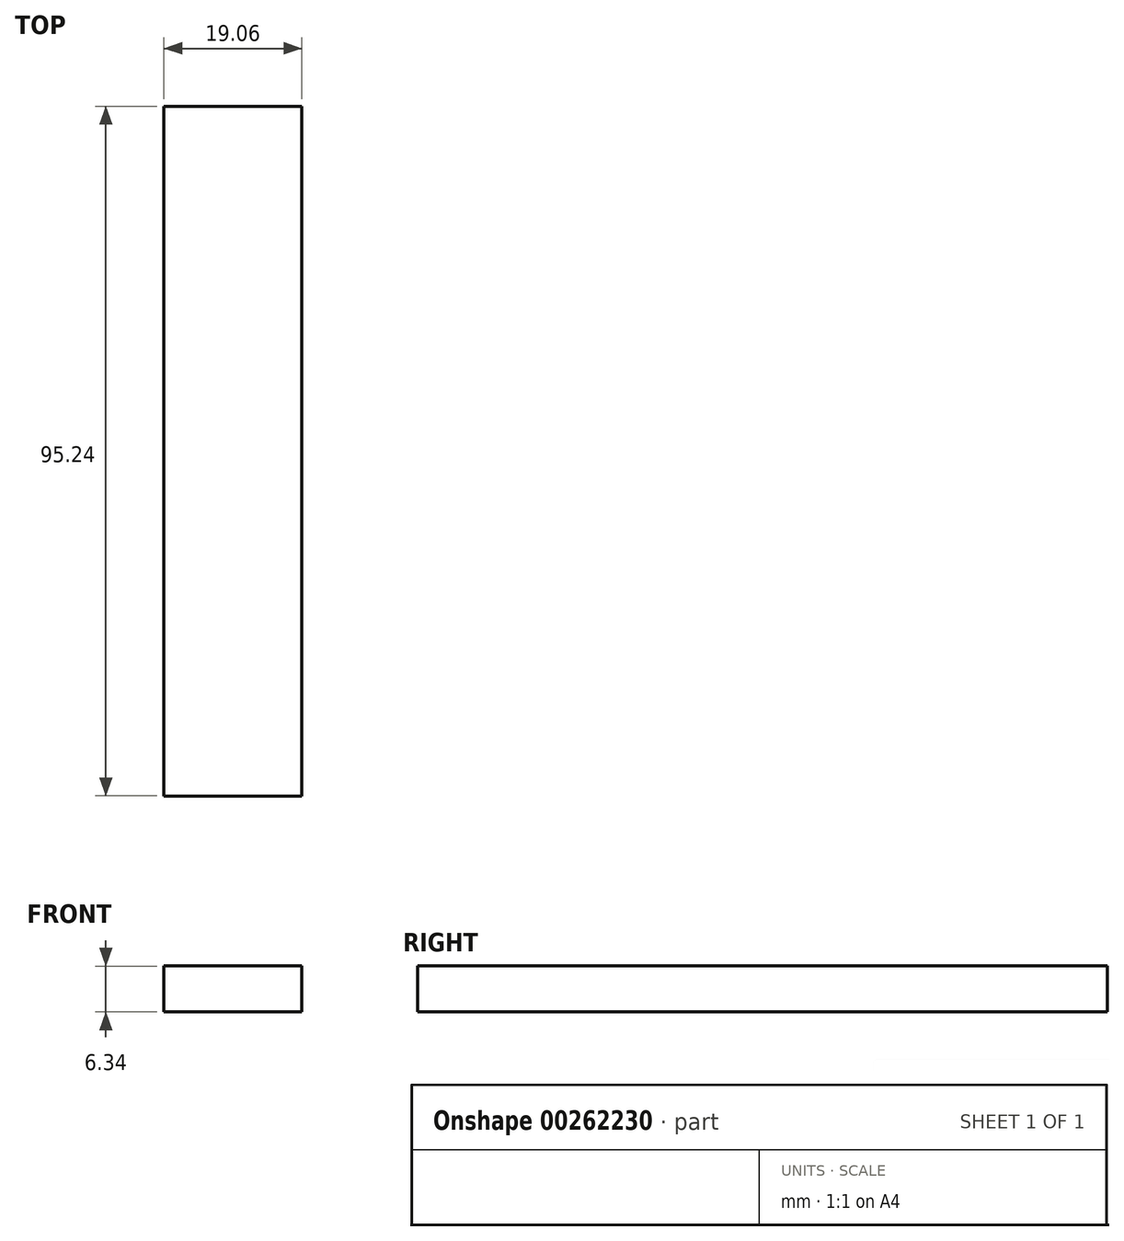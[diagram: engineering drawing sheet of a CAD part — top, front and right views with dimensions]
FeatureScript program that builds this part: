
annotation { "Feature Type Name" : "Feature", "Feature Type Description" : "" }
export const myFeature = defineFeature(function(context is Context, id is Id, definition is map)
    precondition{}
    {
        {
            var Q0;
            Q0=qCreatedBy(makeId("Top.planeOp"),FACE);
            var sketch = newSketch(context, id + "F0", { "sketchPlane" : qUnion([Q0])});
            skLineSegment(sketch, "E0.bottom", {"start": v(9.53, -47.63) * mm, "end": v(-9.52, -47.63) * mm});
            skLineSegment(sketch, "E0.top", {"start": v(9.52, 47.63) * mm, "end": v(-9.53, 47.63) * mm});
            skLineSegment(sketch, "E0.left", {"start": v(9.53, -47.62) * mm, "end": v(9.52, 47.63) * mm});
            skLineSegment(sketch, "E0.right", {"start": v(-9.52, -47.63) * mm, "end": v(-9.53, 47.63) * mm});
            skPoint(sketch, "E0.middle", {"position": v(0, 0) * mm});
            skSolve(sketch);
        }
        {
            var Q0;
            Q0 = qSketchRegion(id + "F0", true);
            extrude(context, id + "F1", {"entities" : qUnion([Q0]), "endBound" : BoundingType.SYMMETRIC, "depth" : 6.35 * mm});
        }
    });
